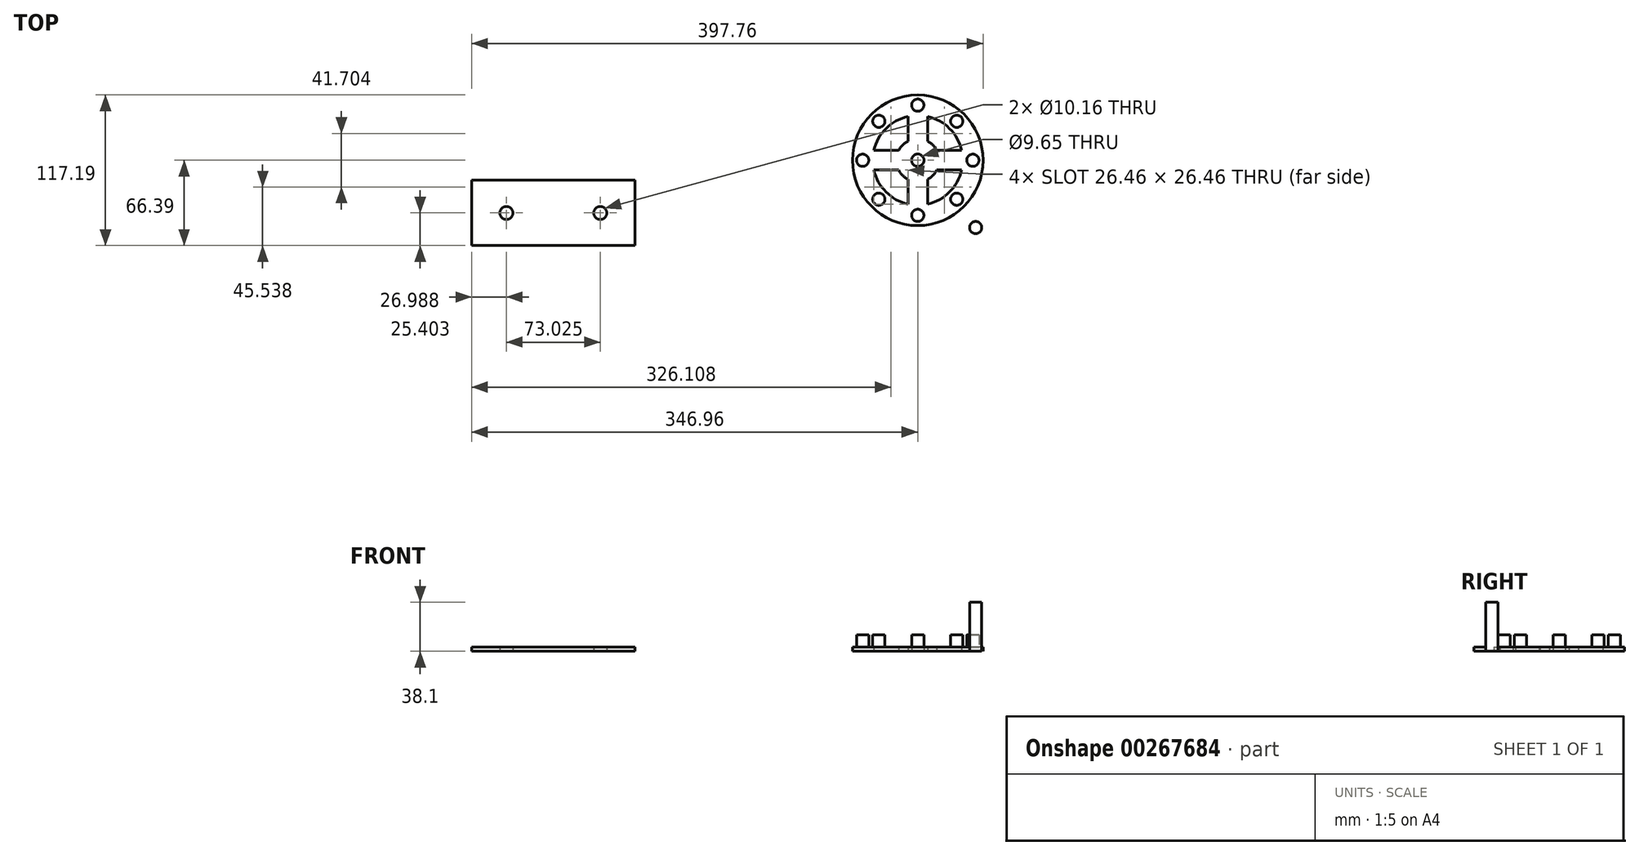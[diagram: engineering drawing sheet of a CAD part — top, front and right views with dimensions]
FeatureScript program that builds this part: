
annotation { "Feature Type Name" : "Feature", "Feature Type Description" : "" }
export const myFeature = defineFeature(function(context is Context, id is Id, definition is map)
    precondition{}
    {
        {
            var Q0;
            Q0=qCreatedBy(makeId("Top.planeOp"),FACE);
            var sketch = newSketch(context, id + "F0", { "sketchPlane" : qUnion([Q0])});
            skCircle(sketch, "E0", {"center": v(0, 0) * mm, "radius": 50.8 * mm});
            skArc(sketch, "E1", {"start": v(34.08, 7.62) * mm, "mid": v(24.7, 24.7) * mm, "end": v(7.62, 34.08) * mm});
            skCircle(sketch, "E2", {"center": v(0, 0) * mm, "radius": 4.83 * mm});
            skArc(sketch, "E3", {"start": v(-7.62, 14.84) * mm, "mid": v(-11.8, 11.8) * mm, "end": v(-14.84, 7.62) * mm});
            skLineSegment(sketch, "E4", {"start": v(-7.62, 34.08) * mm, "end": v(-7.62, 14.84) * mm});
            skLineSegment(sketch, "E5", {"start": v(7.62, 34.08) * mm, "end": v(7.62, 14.84) * mm});
            skLineSegment(sketch, "E6", {"start": v(-34.08, 7.62) * mm, "end": v(-14.84, 7.62) * mm});
            skLineSegment(sketch, "E7", {"start": v(-34.08, -7.62) * mm, "end": v(-14.84, -7.62) * mm});
            skArc(sketch, "E8.trimOffspring", {"start": v(-14.84, -7.62) * mm, "mid": v(-11.8, -11.8) * mm, "end": v(-7.62, -14.84) * mm});
            skArc(sketch, "E9.trimOffspring", {"start": v(7.62, -14.84) * mm, "mid": v(11.8, -11.8) * mm, "end": v(14.84, -7.62) * mm});
            skArc(sketch, "E10.trimOffspring", {"start": v(14.84, 7.62) * mm, "mid": v(11.8, 11.8) * mm, "end": v(7.62, 14.84) * mm});
            skLineSegment(sketch, "E11.trimOffspring", {"start": v(7.62, -14.84) * mm, "end": v(7.62, -34.08) * mm});
            skLineSegment(sketch, "E12.trimOffspring", {"start": v(-7.62, -14.84) * mm, "end": v(-7.62, -34.08) * mm});
            skLineSegment(sketch, "E13.trimOffspring", {"start": v(14.84, 7.62) * mm, "end": v(34.08, 7.62) * mm});
            skLineSegment(sketch, "E14.trimOffspring", {"start": v(14.84, -7.62) * mm, "end": v(34.08, -7.62) * mm});
            skArc(sketch, "E15.trimOffspring", {"start": v(-7.62, 34.08) * mm, "mid": v(-24.7, 24.7) * mm, "end": v(-34.08, 7.62) * mm});
            skArc(sketch, "E16.trimOffspring", {"start": v(7.62, -34.08) * mm, "mid": v(24.7, -24.7) * mm, "end": v(34.08, -7.62) * mm});
            skArc(sketch, "E17.trimOffspring", {"start": v(-34.08, -7.62) * mm, "mid": v(-24.7, -24.7) * mm, "end": v(-7.62, -34.08) * mm});
            skSolve(sketch);
        }
        {
            var Q0;
            Q0=makeQuery(id+"F0.imprint","IMPRINT",FACE,{"disambiguationData":[TD([[makeQuery(id+"F0.imprint","IMPRINT",EDGE,{"derivedFrom":sQuery(id+"F0.wireOp",EDGE,"E0")}),1.0]])]});
            var Q1;
            Q1=makeQuery(id+"F0.imprint","IMPRINT",FACE,{"disambiguationData":[TD([[makeQuery(id+"F0.imprint","IMPRINT",EDGE,{"derivedFrom":sQuery(id+"F0.wireOp",EDGE,"E2")}),-1.0]])]});
            extrude(context, id + "F1", {"entities" : qUnion([Q0, Q1]), "depth" : 3.17 * mm});
        }
        {
            var Q0;
            Q0=qCreatedBy(makeId("Top.planeOp"),FACE);
            var sketch = newSketch(context, id + "F2", { "sketchPlane" : qUnion([Q0])});
            skLineSegment(sketch, "E18.bottom", {"start": v(-346.96, 55.71) * mm, "end": v(-219.96, 55.71) * mm});
            skLineSegment(sketch, "E18.top", {"start": v(-346.96, 4.91) * mm, "end": v(-219.96, 4.91) * mm});
            skLineSegment(sketch, "E18.left", {"start": v(-346.96, 55.71) * mm, "end": v(-346.96, 4.91) * mm});
            skLineSegment(sketch, "E18.right", {"start": v(-219.96, 55.71) * mm, "end": v(-219.96, 4.91) * mm});
            skLineSegment(sketch, "E19.bottom", {"start": v(-346.96, -15.59) * mm, "end": v(-219.96, -15.59) * mm});
            skLineSegment(sketch, "E19.top", {"start": v(-346.96, -66.39) * mm, "end": v(-219.96, -66.39) * mm});
            skLineSegment(sketch, "E19.left", {"start": v(-346.96, -15.59) * mm, "end": v(-346.96, -66.39) * mm});
            skLineSegment(sketch, "E19.right", {"start": v(-219.96, -15.59) * mm, "end": v(-219.96, -66.39) * mm});
            skCircle(sketch, "E20", {"center": v(45.02, -52.38) * mm, "radius": 4.76 * mm});
            skLineSegment(sketch, "E21", {"start": v(-319.97, -15.59) * mm, "end": v(-319.97, -66.39) * mm});
            skLineSegment(sketch, "E22", {"start": v(-246.95, -15.59) * mm, "end": v(-246.95, -66.39) * mm});
            skCircle(sketch, "E23", {"center": v(-319.97, -40.99) * mm, "radius": 5.08 * mm});
            skCircle(sketch, "E24", {"center": v(-246.95, -40.99) * mm, "radius": 5.08 * mm});
            skSolve(sketch);
        }
        {
            var Q0;
            {var subQ0=sQuery(id+"F2.wireOp",EDGE,"E19.left");Q0=makeQuery(id+"F2.imprint","IMPRINT",FACE,{"disambiguationData":[TD([[makeQuery(id+"F2.imprint","IMPRINT",EDGE,{"derivedFrom":subQ0}),1.0]])]});}
            var Q1;
            {var subQ0=sQuery(id+"F2.wireOp",EDGE,"E21");var subQ10=sQuery(id+"F2.wireOp",EDGE,"E19.bottom");var subQ11=makeQuery(id+"F2.imprint","INTERSECT",VERTEX,{"derivedFrom":[subQ10,subQ0]});Q1=makeQuery(id+"F2.imprint","IMPRINT",FACE,{"disambiguationData":[TD([[makeQuery(id+"F2.imprint","IMPRINT",EDGE,{"disambiguationData":[TD([[subQ11,-1.0]])],"derivedFrom":subQ10}),-1.0]])]});}
            var Q2;
            {var subQ5=sQuery(id+"F2.wireOp",EDGE,"E19.right");Q2=makeQuery(id+"F2.imprint","IMPRINT",FACE,{"disambiguationData":[TD([[makeQuery(id+"F2.imprint","IMPRINT",EDGE,{"derivedFrom":subQ5}),-1.0]])]});}
            extrude(context, id + "F3", {"entities" : qUnion([Q0, Q1, Q2]), "depth" : 3.17 * mm});
        }
        {
            var Q0;
            Q0=makeQuery(id+"F2.imprint","IMPRINT",FACE,{"disambiguationData":[TD([[makeQuery(id+"F2.imprint","IMPRINT",EDGE,{"derivedFrom":sQuery(id+"F2.wireOp",EDGE,"E20")}),1.0]])]});
            extrude(context, id + "F4", {"entities" : qUnion([Q0]), "depth" : 38.1 * mm});
        }
        {
            var Q0;
            Q0=makeQuery(id+"F1.opExtrude","CAP_FACE",FACE,{"disambiguationData":[OSD([sQuery(id+"F0.wireOp",EDGE,"E0"),sQuery(id+"F0.wireOp",EDGE,"E1"),sQuery(id+"F0.wireOp",EDGE,"E2"),sQuery(id+"F0.wireOp",EDGE,"E3"),sQuery(id+"F0.wireOp",EDGE,"E4"),sQuery(id+"F0.wireOp",EDGE,"E5"),sQuery(id+"F0.wireOp",EDGE,"E6"),sQuery(id+"F0.wireOp",EDGE,"E7"),sQuery(id+"F0.wireOp",EDGE,"E8.trimOffspring"),sQuery(id+"F0.wireOp",EDGE,"E9.trimOffspring"),sQuery(id+"F0.wireOp",EDGE,"E10.trimOffspring"),sQuery(id+"F0.wireOp",EDGE,"E11.trimOffspring"),sQuery(id+"F0.wireOp",EDGE,"E12.trimOffspring"),sQuery(id+"F0.wireOp",EDGE,"E13.trimOffspring"),sQuery(id+"F0.wireOp",EDGE,"E14.trimOffspring"),sQuery(id+"F0.wireOp",EDGE,"E15.trimOffspring"),sQuery(id+"F0.wireOp",EDGE,"E16.trimOffspring"),sQuery(id+"F0.wireOp",EDGE,"E17.trimOffspring")])],"isStart":false});
            var sketch = newSketch(context, id + "F5", { "sketchPlane" : qUnion([Q0])});
            skCircle(sketch, "E25", {"center": v(0, 0) * mm, "radius": 42.86 * mm});
            skLineSegment(sketch, "E26", {"start": v(0, 0) * mm, "end": v(0, 50.8) * mm});
            skCircle(sketch, "E27", {"center": v(0, 42.86) * mm, "radius": 4.76 * mm});
            skCircle(sketch, "E28", {"center": v(42.86, 0) * mm, "radius": 4.76 * mm});
            skCircle(sketch, "E29", {"center": v(0, -42.86) * mm, "radius": 4.76 * mm});
            skCircle(sketch, "E30", {"center": v(-42.86, 0) * mm, "radius": 4.76 * mm});
            skLineSegment(sketch, "E31", {"start": v(0, 0) * mm, "end": v(30.3, 30.3) * mm});
            skLineSegment(sketch, "E32", {"start": v(-30.3, 30.3) * mm, "end": v(30.3, -30.3) * mm});
            skLineSegment(sketch, "E33", {"start": v(0, 0) * mm, "end": v(-30.3, -30.3) * mm});
            skCircle(sketch, "E34", {"center": v(-30.3, 30.3) * mm, "radius": 4.76 * mm});
            skCircle(sketch, "E35", {"center": v(30.3, 30.3) * mm, "radius": 4.76 * mm});
            skCircle(sketch, "E36", {"center": v(-30.3, -30.3) * mm, "radius": 4.76 * mm});
            skCircle(sketch, "E37", {"center": v(30.3, -30.3) * mm, "radius": 4.76 * mm});
            skSolve(sketch);
        }
        {
            var Q0;
            {var subQ0=sQuery(id+"F5.wireOp",EDGE,"E30");var subQ1=sQuery(id+"F5.wireOp",EDGE,"E25");var subQ2=makeQuery(id+"F5.imprint","INTERSECT",VERTEX,{"disambiguationData":[OD(0.0)],"derivedFrom":[subQ1,subQ0]});Q0=makeQuery(id+"F5.imprint","IMPRINT",FACE,{"disambiguationData":[TD([[makeQuery(id+"F5.imprint","IMPRINT",EDGE,{"disambiguationData":[TD([[subQ2,-1.0]])],"derivedFrom":subQ1}),-1.0]])]});}
            var Q1;
            {var subQ0=sQuery(id+"F5.wireOp",EDGE,"E30");var subQ1=sQuery(id+"F5.wireOp",EDGE,"E25");var subQ2=makeQuery(id+"F5.imprint","INTERSECT",VERTEX,{"disambiguationData":[OD(0.0)],"derivedFrom":[subQ1,subQ0]});Q1=makeQuery(id+"F5.imprint","IMPRINT",FACE,{"disambiguationData":[TD([[makeQuery(id+"F5.imprint","IMPRINT",EDGE,{"disambiguationData":[TD([[subQ2,-1.0]])],"derivedFrom":subQ1}),1.0]])]});}
            var Q2;
            {var subQ0=sQuery(id+"F5.wireOp",EDGE,"E25");var subQ1=makeQuery(id+"F5.imprint","INTERSECT",VERTEX,{"disambiguationData":[OD(0.0)],"derivedFrom":[subQ0,sQuery(id+"F5.wireOp",EDGE,"E32")]});Q2=makeQuery(id+"F5.imprint","IMPRINT",FACE,{"disambiguationData":[TD([[makeQuery(id+"F5.imprint","IMPRINT",EDGE,{"disambiguationData":[TD([[subQ1,1.0]])],"derivedFrom":subQ0}),-1.0]])]});}
            var Q3;
            {var subQ0=sQuery(id+"F5.wireOp",EDGE,"E32");var subQ1=sQuery(id+"F5.wireOp",EDGE,"E25");var subQ2=makeQuery(id+"F5.imprint","INTERSECT",VERTEX,{"disambiguationData":[OD(0.0)],"derivedFrom":[subQ1,subQ0]});Q3=makeQuery(id+"F5.imprint","IMPRINT",FACE,{"disambiguationData":[TD([[makeQuery(id+"F5.imprint","IMPRINT",EDGE,{"disambiguationData":[TD([[subQ2,1.0]])],"derivedFrom":subQ1}),1.0]])]});}
            var Q4;
            {var subQ0=sQuery(id+"F5.wireOp",EDGE,"E32");var subQ1=sQuery(id+"F5.wireOp",EDGE,"E25");var subQ2=makeQuery(id+"F5.imprint","INTERSECT",VERTEX,{"disambiguationData":[OD(0.0)],"derivedFrom":[subQ1,subQ0]});Q4=makeQuery(id+"F5.imprint","IMPRINT",FACE,{"disambiguationData":[TD([[makeQuery(id+"F5.imprint","IMPRINT",EDGE,{"disambiguationData":[TD([[subQ2,-1.0]])],"derivedFrom":subQ1}),1.0]])]});}
            var Q5;
            {var subQ0=sQuery(id+"F5.wireOp",EDGE,"E26");var subQ1=sQuery(id+"F5.wireOp",EDGE,"E25");var subQ2=makeQuery(id+"F5.imprint","INTERSECT",VERTEX,{"derivedFrom":[subQ1,subQ0]});Q5=makeQuery(id+"F5.imprint","IMPRINT",FACE,{"disambiguationData":[TD([[makeQuery(id+"F5.imprint","IMPRINT",EDGE,{"disambiguationData":[TD([[subQ2,-1.0]])],"derivedFrom":subQ1}),-1.0]])]});}
            var Q6;
            {var subQ0=sQuery(id+"F5.wireOp",EDGE,"E27");var subQ1=sQuery(id+"F5.wireOp",EDGE,"E25");var subQ2=makeQuery(id+"F5.imprint","INTERSECT",VERTEX,{"disambiguationData":[OD(0.0)],"derivedFrom":[subQ1,subQ0]});Q6=makeQuery(id+"F5.imprint","IMPRINT",FACE,{"disambiguationData":[TD([[makeQuery(id+"F5.imprint","IMPRINT",EDGE,{"disambiguationData":[TD([[subQ2,-1.0]])],"derivedFrom":subQ1}),-1.0]])]});}
            var Q7;
            {var subQ0=sQuery(id+"F5.wireOp",EDGE,"E27");var subQ1=sQuery(id+"F5.wireOp",EDGE,"E25");var subQ2=makeQuery(id+"F5.imprint","INTERSECT",VERTEX,{"disambiguationData":[OD(0.0)],"derivedFrom":[subQ1,subQ0]});Q7=makeQuery(id+"F5.imprint","IMPRINT",FACE,{"disambiguationData":[TD([[makeQuery(id+"F5.imprint","IMPRINT",EDGE,{"disambiguationData":[TD([[subQ2,-1.0]])],"derivedFrom":subQ1}),1.0]])]});}
            var Q8;
            {var subQ0=sQuery(id+"F5.wireOp",EDGE,"E26");var subQ1=sQuery(id+"F5.wireOp",EDGE,"E25");var subQ2=makeQuery(id+"F5.imprint","INTERSECT",VERTEX,{"derivedFrom":[subQ1,subQ0]});Q8=makeQuery(id+"F5.imprint","IMPRINT",FACE,{"disambiguationData":[TD([[makeQuery(id+"F5.imprint","IMPRINT",EDGE,{"disambiguationData":[TD([[subQ2,-1.0]])],"derivedFrom":subQ1}),1.0]])]});}
            var Q9;
            {var subQ0=sQuery(id+"F5.wireOp",EDGE,"E31");var subQ1=sQuery(id+"F5.wireOp",EDGE,"E25");var subQ2=makeQuery(id+"F5.imprint","INTERSECT",VERTEX,{"derivedFrom":[subQ1,subQ0]});Q9=makeQuery(id+"F5.imprint","IMPRINT",FACE,{"disambiguationData":[TD([[makeQuery(id+"F5.imprint","IMPRINT",EDGE,{"disambiguationData":[TD([[subQ2,-1.0]])],"derivedFrom":subQ1}),1.0]])]});}
            var Q10;
            {var subQ0=sQuery(id+"F5.wireOp",EDGE,"E25");var subQ1=makeQuery(id+"F5.imprint","INTERSECT",VERTEX,{"derivedFrom":[subQ0,sQuery(id+"F5.wireOp",EDGE,"E31")]});Q10=makeQuery(id+"F5.imprint","IMPRINT",FACE,{"disambiguationData":[TD([[makeQuery(id+"F5.imprint","IMPRINT",EDGE,{"disambiguationData":[TD([[subQ1,1.0]])],"derivedFrom":subQ0}),-1.0]])]});}
            var Q11;
            {var subQ0=sQuery(id+"F5.wireOp",EDGE,"E31");var subQ1=sQuery(id+"F5.wireOp",EDGE,"E25");var subQ2=makeQuery(id+"F5.imprint","INTERSECT",VERTEX,{"derivedFrom":[subQ1,subQ0]});Q11=makeQuery(id+"F5.imprint","IMPRINT",FACE,{"disambiguationData":[TD([[makeQuery(id+"F5.imprint","IMPRINT",EDGE,{"disambiguationData":[TD([[subQ2,1.0]])],"derivedFrom":subQ1}),1.0]])]});}
            var Q12;
            {var subQ0=sQuery(id+"F5.wireOp",EDGE,"E28");var subQ1=sQuery(id+"F5.wireOp",EDGE,"E25");var subQ2=makeQuery(id+"F5.imprint","INTERSECT",VERTEX,{"disambiguationData":[OD(0.0)],"derivedFrom":[subQ1,subQ0]});Q12=makeQuery(id+"F5.imprint","IMPRINT",FACE,{"disambiguationData":[TD([[makeQuery(id+"F5.imprint","IMPRINT",EDGE,{"disambiguationData":[TD([[subQ2,1.0]])],"derivedFrom":subQ1}),1.0]])]});}
            var Q13;
            {var subQ0=sQuery(id+"F5.wireOp",EDGE,"E28");var subQ1=sQuery(id+"F5.wireOp",EDGE,"E25");var subQ2=makeQuery(id+"F5.imprint","INTERSECT",VERTEX,{"disambiguationData":[OD(0.0)],"derivedFrom":[subQ1,subQ0]});Q13=makeQuery(id+"F5.imprint","IMPRINT",FACE,{"disambiguationData":[TD([[makeQuery(id+"F5.imprint","IMPRINT",EDGE,{"disambiguationData":[TD([[subQ2,1.0]])],"derivedFrom":subQ1}),-1.0]])]});}
            var Q14;
            {var subQ0=sQuery(id+"F5.wireOp",EDGE,"E25");var subQ1=makeQuery(id+"F5.imprint","INTERSECT",VERTEX,{"derivedFrom":[subQ0,sQuery(id+"F5.wireOp",EDGE,"E33")]});Q14=makeQuery(id+"F5.imprint","IMPRINT",FACE,{"disambiguationData":[TD([[makeQuery(id+"F5.imprint","IMPRINT",EDGE,{"disambiguationData":[TD([[subQ1,1.0]])],"derivedFrom":subQ0}),-1.0]])]});}
            var Q15;
            {var subQ0=sQuery(id+"F5.wireOp",EDGE,"E33");var subQ1=sQuery(id+"F5.wireOp",EDGE,"E25");var subQ2=makeQuery(id+"F5.imprint","INTERSECT",VERTEX,{"derivedFrom":[subQ1,subQ0]});Q15=makeQuery(id+"F5.imprint","IMPRINT",FACE,{"disambiguationData":[TD([[makeQuery(id+"F5.imprint","IMPRINT",EDGE,{"disambiguationData":[TD([[subQ2,-1.0]])],"derivedFrom":subQ1}),1.0]])]});}
            var Q16;
            {var subQ0=sQuery(id+"F5.wireOp",EDGE,"E33");var subQ1=sQuery(id+"F5.wireOp",EDGE,"E25");var subQ2=makeQuery(id+"F5.imprint","INTERSECT",VERTEX,{"derivedFrom":[subQ1,subQ0]});Q16=makeQuery(id+"F5.imprint","IMPRINT",FACE,{"disambiguationData":[TD([[makeQuery(id+"F5.imprint","IMPRINT",EDGE,{"disambiguationData":[TD([[subQ2,1.0]])],"derivedFrom":subQ1}),1.0]])]});}
            var Q17;
            {var subQ0=sQuery(id+"F5.wireOp",EDGE,"E29");var subQ1=sQuery(id+"F5.wireOp",EDGE,"E25");var subQ2=makeQuery(id+"F5.imprint","INTERSECT",VERTEX,{"disambiguationData":[OD(0.0)],"derivedFrom":[subQ1,subQ0]});Q17=makeQuery(id+"F5.imprint","IMPRINT",FACE,{"disambiguationData":[TD([[makeQuery(id+"F5.imprint","IMPRINT",EDGE,{"disambiguationData":[TD([[subQ2,-1.0]])],"derivedFrom":subQ1}),1.0]])]});}
            var Q18;
            {var subQ0=sQuery(id+"F5.wireOp",EDGE,"E29");var subQ1=sQuery(id+"F5.wireOp",EDGE,"E25");var subQ2=makeQuery(id+"F5.imprint","INTERSECT",VERTEX,{"disambiguationData":[OD(0.0)],"derivedFrom":[subQ1,subQ0]});Q18=makeQuery(id+"F5.imprint","IMPRINT",FACE,{"disambiguationData":[TD([[makeQuery(id+"F5.imprint","IMPRINT",EDGE,{"disambiguationData":[TD([[subQ2,-1.0]])],"derivedFrom":subQ1}),-1.0]])]});}
            var Q19;
            {var subQ0=sQuery(id+"F5.wireOp",EDGE,"E32");var subQ1=sQuery(id+"F5.wireOp",EDGE,"E25");var subQ2=makeQuery(id+"F5.imprint","INTERSECT",VERTEX,{"disambiguationData":[OD(1.0)],"derivedFrom":[subQ1,subQ0]});Q19=makeQuery(id+"F5.imprint","IMPRINT",FACE,{"disambiguationData":[TD([[makeQuery(id+"F5.imprint","IMPRINT",EDGE,{"disambiguationData":[TD([[subQ2,1.0]])],"derivedFrom":subQ1}),1.0]])]});}
            var Q20;
            {var subQ0=sQuery(id+"F5.wireOp",EDGE,"E32");var subQ1=sQuery(id+"F5.wireOp",EDGE,"E25");var subQ2=makeQuery(id+"F5.imprint","INTERSECT",VERTEX,{"disambiguationData":[OD(1.0)],"derivedFrom":[subQ1,subQ0]});Q20=makeQuery(id+"F5.imprint","IMPRINT",FACE,{"disambiguationData":[TD([[makeQuery(id+"F5.imprint","IMPRINT",EDGE,{"disambiguationData":[TD([[subQ2,-1.0]])],"derivedFrom":subQ1}),1.0]])]});}
            var Q21;
            {var subQ0=sQuery(id+"F5.wireOp",EDGE,"E25");var subQ1=makeQuery(id+"F5.imprint","INTERSECT",VERTEX,{"disambiguationData":[OD(1.0)],"derivedFrom":[subQ0,sQuery(id+"F5.wireOp",EDGE,"E32")]});Q21=makeQuery(id+"F5.imprint","IMPRINT",FACE,{"disambiguationData":[TD([[makeQuery(id+"F5.imprint","IMPRINT",EDGE,{"disambiguationData":[TD([[subQ1,1.0]])],"derivedFrom":subQ0}),-1.0]])]});}
            extrude(context, id + "F6", {"entities" : qUnion([Q0, Q1, Q2, Q3, Q4, Q5, Q6, Q7, Q8, Q9, Q10, Q11, Q12, Q13, Q14, Q15, Q16, Q17, Q18, Q19, Q20, Q21]), "operationType" : NewBodyOperationType.ADD, "depth" : 9.52 * mm});
        }
        {
            var Q0;
            Q0=qCreatedBy(makeId("Top.planeOp"),FACE);
            var sketch = newSketch(context, id + "F7", { "sketchPlane" : qUnion([Q0])});
            skLineSegment(sketch, "E38.bottom", {"start": v(-284.81, -127.57) * mm, "end": v(-157.81, -127.57) * mm});
            skLineSegment(sketch, "E38.top", {"start": v(-284.81, -178.37) * mm, "end": v(-157.81, -178.37) * mm});
            skLineSegment(sketch, "E38.left", {"start": v(-284.81, -127.57) * mm, "end": v(-284.81, -178.37) * mm});
            skLineSegment(sketch, "E38.right", {"start": v(-157.81, -127.57) * mm, "end": v(-157.81, -178.37) * mm});
            skLineSegment(sketch, "E39", {"start": v(-284.81, -152.97) * mm, "end": v(-157.81, -152.97) * mm});
            skLineSegment(sketch, "E40", {"start": v(-259.41, -127.57) * mm, "end": v(-259.41, -178.37) * mm});
            skLineSegment(sketch, "E41", {"start": v(-183.21, -127.57) * mm, "end": v(-183.21, -178.37) * mm});
            skCircle(sketch, "E42", {"center": v(-259.41, -152.97) * mm, "radius": 4.83 * mm});
            skCircle(sketch, "E43", {"center": v(-183.21, -152.97) * mm, "radius": 4.83 * mm});
            skSolve(sketch);
        }
        {
            var Q0;
            {var subQ0=sQuery(id+"F7.wireOp",EDGE,"E40");var subQ1=sQuery(id+"F7.wireOp",EDGE,"E38.bottom");var subQ2=makeQuery(id+"F7.imprint","INTERSECT",VERTEX,{"derivedFrom":[subQ1,subQ0]});Q0=makeQuery(id+"F7.imprint","IMPRINT",FACE,{"disambiguationData":[TD([[makeQuery(id+"F7.imprint","IMPRINT",EDGE,{"disambiguationData":[TD([[subQ2,-1.0]])],"derivedFrom":subQ1}),-1.0]])]});}
            var Q1;
            {var subQ0=sQuery(id+"F7.wireOp",EDGE,"E40");var subQ1=sQuery(id+"F7.wireOp",EDGE,"E38.top");var subQ2=makeQuery(id+"F7.imprint","INTERSECT",VERTEX,{"derivedFrom":[subQ1,subQ0]});Q1=makeQuery(id+"F7.imprint","IMPRINT",FACE,{"disambiguationData":[TD([[makeQuery(id+"F7.imprint","IMPRINT",EDGE,{"disambiguationData":[TD([[subQ2,-1.0]])],"derivedFrom":subQ1}),1.0]])]});}
            var Q2;
            {var subQ1=sQuery(id+"F7.wireOp",EDGE,"E38.top");var subQ6=sQuery(id+"F7.wireOp",EDGE,"E38.left");var subQ9=makeQuery(id+"F7.imprint","INTERSECT",VERTEX,{"derivedFrom":[subQ1,subQ6]});Q2=makeQuery(id+"F7.imprint","IMPRINT",FACE,{"disambiguationData":[TD([[makeQuery(id+"F7.imprint","IMPRINT",EDGE,{"disambiguationData":[TD([[subQ9,-1.0]])],"derivedFrom":subQ1}),1.0]])]});}
            var Q3;
            {var subQ1=sQuery(id+"F7.wireOp",EDGE,"E38.bottom");var subQ5=sQuery(id+"F7.wireOp",EDGE,"E38.left");var subQ6=makeQuery(id+"F7.imprint","INTERSECT",VERTEX,{"derivedFrom":[subQ1,subQ5]});Q3=makeQuery(id+"F7.imprint","IMPRINT",FACE,{"disambiguationData":[TD([[makeQuery(id+"F7.imprint","IMPRINT",EDGE,{"disambiguationData":[TD([[subQ6,-1.0]])],"derivedFrom":subQ1}),-1.0]])]});}
            var Q4;
            {var subQ1=sQuery(id+"F7.wireOp",EDGE,"E38.bottom");var subQ6=sQuery(id+"F7.wireOp",EDGE,"E38.right");var subQ9=makeQuery(id+"F7.imprint","INTERSECT",VERTEX,{"derivedFrom":[subQ1,subQ6]});Q4=makeQuery(id+"F7.imprint","IMPRINT",FACE,{"disambiguationData":[TD([[makeQuery(id+"F7.imprint","IMPRINT",EDGE,{"disambiguationData":[TD([[subQ9,1.0]])],"derivedFrom":subQ1}),-1.0]])]});}
            var Q5;
            {var subQ1=sQuery(id+"F7.wireOp",EDGE,"E38.right");var subQ5=sQuery(id+"F7.wireOp",EDGE,"E38.top");var subQ6=makeQuery(id+"F7.imprint","INTERSECT",VERTEX,{"derivedFrom":[subQ5,subQ1]});Q5=makeQuery(id+"F7.imprint","IMPRINT",FACE,{"disambiguationData":[TD([[makeQuery(id+"F7.imprint","IMPRINT",EDGE,{"disambiguationData":[TD([[subQ6,1.0]])],"derivedFrom":subQ5}),1.0]])]});}
            extrude(context, id + "F8", {"entities" : qUnion([Q0, Q1, Q2, Q3, Q4, Q5]), "depth" : 3.17 * mm});
        }
        {
            var Q0;
            Q0=makeQuery(id+"F8.opExtrude","SWEPT_BODY",BODY,{"disambiguationData":[OSD([sQuery(id+"F7.wireOp",EDGE,"E38.bottom"),sQuery(id+"F7.wireOp",EDGE,"E38.top"),sQuery(id+"F7.wireOp",EDGE,"E38.left"),sQuery(id+"F7.wireOp",EDGE,"E38.right"),sQuery(id+"F7.wireOp",EDGE,"E42"),sQuery(id+"F7.wireOp",EDGE,"E43")])]});
            deleteBodies(context, id + "F9", {"entities" : qUnion([Q0])});
        }
        {
            var Q0;
            Q0=makeQuery(id+"F3.opExtrude","SWEPT_BODY",BODY,{"disambiguationData":[OSD([sQuery(id+"F2.wireOp",EDGE,"E19.bottom"),sQuery(id+"F2.wireOp",EDGE,"E19.top"),sQuery(id+"F2.wireOp",EDGE,"E19.left"),sQuery(id+"F2.wireOp",EDGE,"E19.right"),sQuery(id+"F2.wireOp",EDGE,"E23"),sQuery(id+"F2.wireOp",EDGE,"E24")])]});
            deleteBodies(context, id + "F10", {"entities" : qUnion([Q0])});
        }
        {
            var Q0;
            {var subQ5=sQuery(id+"F2.wireOp",EDGE,"E19.left");Q0=makeQuery(id+"F2.imprint","IMPRINT",FACE,{"disambiguationData":[TD([[makeQuery(id+"F2.imprint","IMPRINT",EDGE,{"derivedFrom":subQ5}),1.0]])]});}
            var Q1;
            {var subQ0=sQuery(id+"F2.wireOp",EDGE,"E19.right");Q1=makeQuery(id+"F2.imprint","IMPRINT",FACE,{"disambiguationData":[TD([[makeQuery(id+"F2.imprint","IMPRINT",EDGE,{"derivedFrom":subQ0}),-1.0]])]});}
            var Q2;
            {var subQ0=sQuery(id+"F2.wireOp",EDGE,"E21");var subQ1=sQuery(id+"F2.wireOp",EDGE,"E19.bottom");var subQ2=makeQuery(id+"F2.imprint","INTERSECT",VERTEX,{"derivedFrom":[subQ1,subQ0]});Q2=makeQuery(id+"F2.imprint","IMPRINT",FACE,{"disambiguationData":[TD([[makeQuery(id+"F2.imprint","IMPRINT",EDGE,{"disambiguationData":[TD([[subQ2,-1.0]])],"derivedFrom":subQ1}),-1.0]])]});}
            extrude(context, id + "F11", {"entities" : qUnion([Q0, Q1, Q2]), "depth" : 3.17 * mm});
        }
    });
